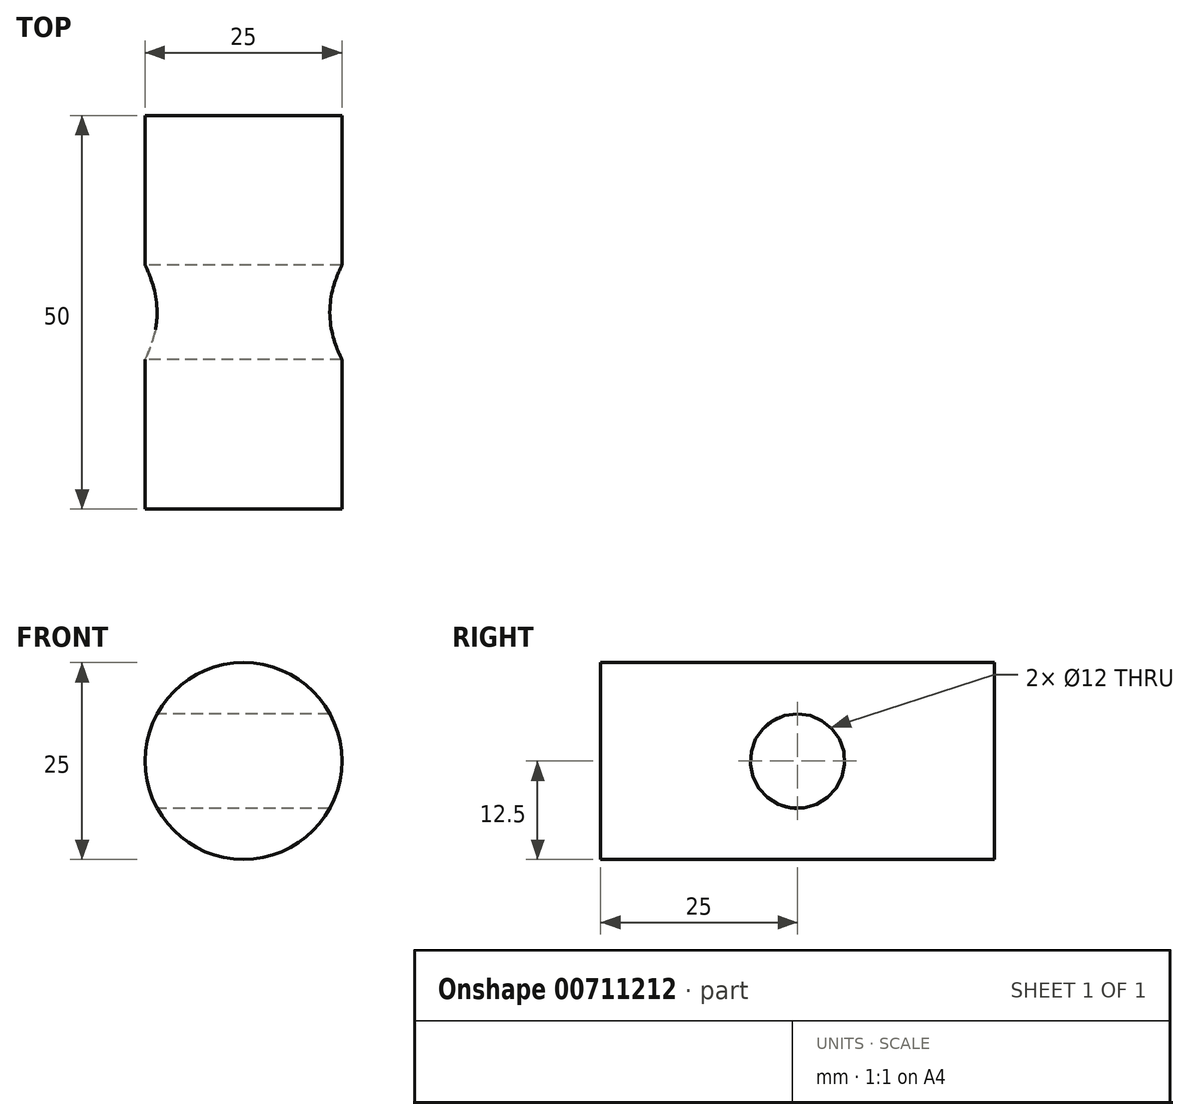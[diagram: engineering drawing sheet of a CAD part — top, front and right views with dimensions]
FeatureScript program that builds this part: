
annotation { "Feature Type Name" : "Feature", "Feature Type Description" : "" }
export const myFeature = defineFeature(function(context is Context, id is Id, definition is map)
    precondition{}
    {
        {
            var Q0;
            Q0=qCreatedBy(makeId("Front.planeOp"),FACE);
            var sketch = newSketch(context, id + "F0", { "sketchPlane" : qUnion([Q0])});
            skCircle(sketch, "E0", {"center": v(0, 0) * mm, "radius": 12.5 * mm});
            skSolve(sketch);
        }
        {
            var Q0;
            Q0=qCreatedBy(makeId("Right.planeOp"),FACE);
            var sketch = newSketch(context, id + "F1", { "sketchPlane" : qUnion([Q0])});
            skCircle(sketch, "E1", {"center": v(0, 0) * mm, "radius": 6 * mm});
            skSolve(sketch);
        }
        {
            var Q0;
            Q0=makeQuery(id+"F0.imprint","IMPRINT",FACE,{"disambiguationData":[TD([[makeQuery(id+"F0.imprint","IMPRINT",EDGE,{"derivedFrom":sQuery(id+"F0.wireOp",EDGE,"E0")}),1.0]])]});
            var Q1;
            Q1 = qSketchRegion(id + "F0", true);
            extrude(context, id + "F2", {"entities" : qUnion([Q0, Q1]), "endBound" : BoundingType.SYMMETRIC, "depth" : 50 * mm, "offsetDistance" : 25 * mm});
        }
        {
            var Q0;
            Q0=sQuery(id+"F1.wireOp",VERTEX,"E1.center");
            var Q1;
            Q1=makeQuery(id+"F2.opExtrude","SWEPT_BODY",BODY,{"disambiguationData":[OSD([sQuery(id+"F0.wireOp",EDGE,"E0")])]});
            hole(context, id + "F3", {"style" : HoleStyle.SIMPLE, "endStyle" : HoleEndStyle.THROUGH, "oppositeDirection" : true, "holeDiameter" : 12 * mm, "majorDiameter" : 5 * mm, "isTappedThrough" : true, "tappedDepth" : 12 * mm, "tapClearance" : 3, "locations" : qUnion([Q0]), "scope" : qUnion([Q1])});
        }
        {
            var Q0;
            Q0=sQuery(id+"F1.wireOp",VERTEX,"E1.center");
            var Q1;
            Q1=makeQuery(id+"F2.opExtrude","SWEPT_BODY",BODY,{"disambiguationData":[OSD([sQuery(id+"F0.wireOp",EDGE,"E0")])]});
            hole(context, id + "F4", {"style" : HoleStyle.SIMPLE, "endStyle" : HoleEndStyle.THROUGH, "holeDiameter" : 12 * mm, "majorDiameter" : 5 * mm, "isTappedThrough" : true, "tappedDepth" : 12 * mm, "tapClearance" : 3, "locations" : qUnion([Q0]), "scope" : qUnion([Q1])});
        }
    });
